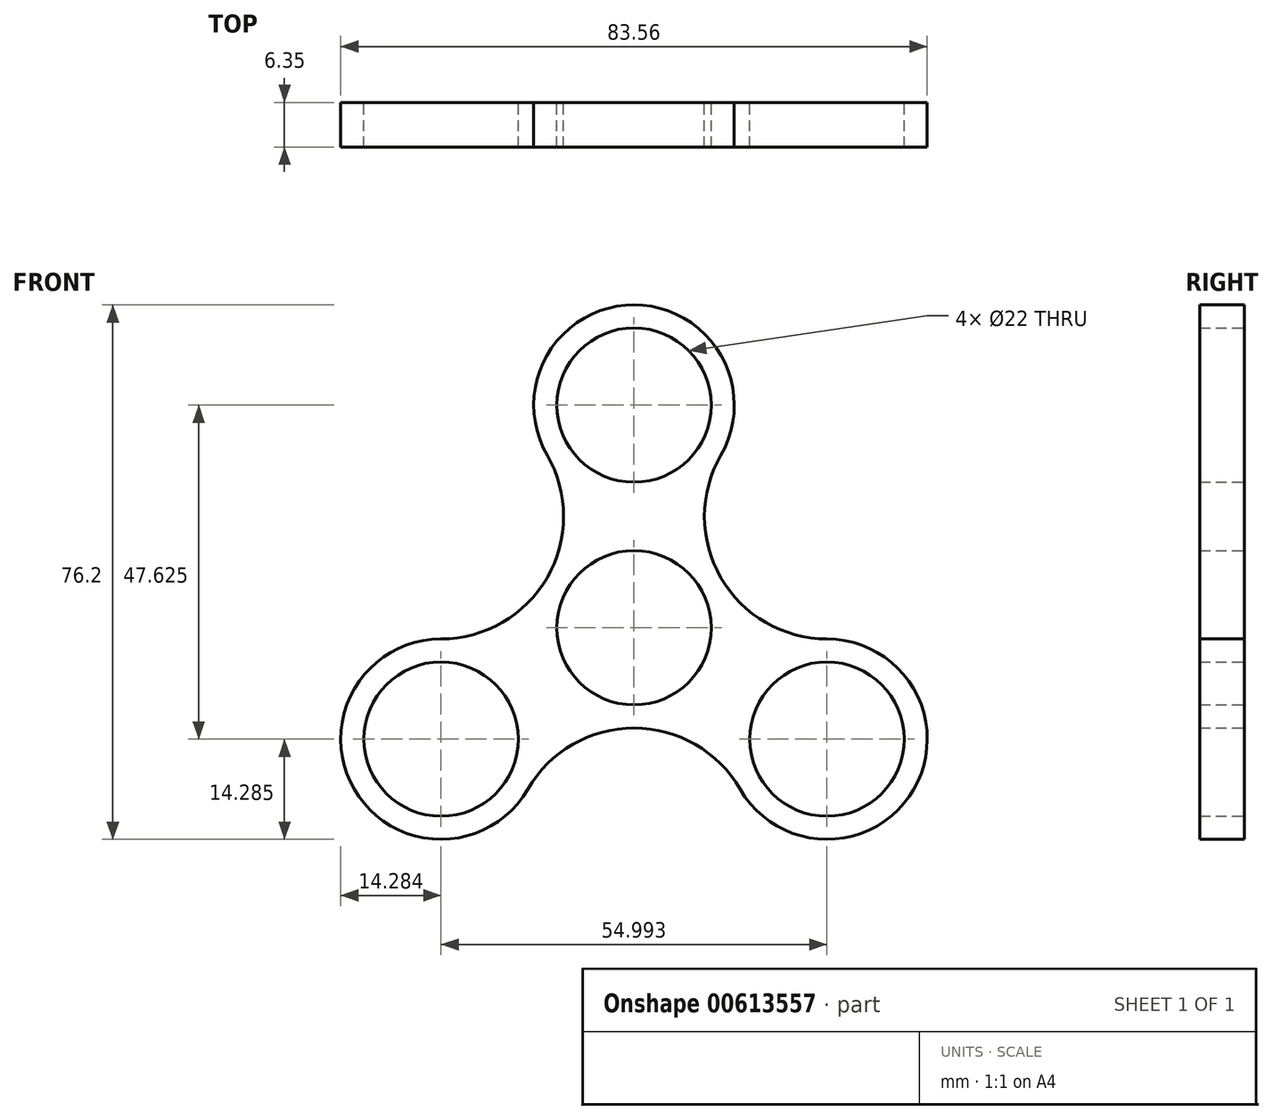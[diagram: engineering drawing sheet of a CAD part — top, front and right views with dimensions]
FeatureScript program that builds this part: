
annotation { "Feature Type Name" : "Feature", "Feature Type Description" : "" }
export const myFeature = defineFeature(function(context is Context, id is Id, definition is map)
    precondition{}
    {
        {
            var Q0;
            Q0=qCreatedBy(makeId("Front.planeOp"),FACE);
            var sketch = newSketch(context, id + "F0", { "sketchPlane" : qUnion([Q0])});
            skCircle(sketch, "E0", {"center": v(0, 0) * mm, "radius": 14.29 * mm});
            skCircle(sketch, "E1", {"center": v(0, 31.75) * mm, "radius": 14.29 * mm});
            skCircle(sketch, "E2", {"center": v(0, 31.75) * mm, "radius": 11 * mm});
            skCircle(sketch, "E3", {"center": v(0, 0) * mm, "radius": 11 * mm});
            skCircle(sketch, "E4.1.2", {"center": v(-27.5, -15.87) * mm, "radius": 14.29 * mm});
            skCircle(sketch, "E4.1.3", {"center": v(-27.5, -15.87) * mm, "radius": 11 * mm});
            skCircle(sketch, "E4.2.2", {"center": v(27.5, -15.88) * mm, "radius": 14.29 * mm});
            skCircle(sketch, "E4.2.3", {"center": v(27.5, -15.88) * mm, "radius": 11 * mm});
            skArc(sketch, "E5", {"start": v(-27.5, -1.59) * mm, "mid": v(-12.37, 7.14) * mm, "end": v(-12.37, 24.6) * mm});
            skArc(sketch, "E6", {"start": v(12.37, 24.6) * mm, "mid": v(12.37, 7.14) * mm, "end": v(27.5, -1.59) * mm});
            skArc(sketch, "E7", {"start": v(15.12, -23.02) * mm, "mid": v(0, -14.29) * mm, "end": v(-15.12, -23.02) * mm});
            skSolve(sketch);
        }
        {
            var Q0;
            {var subQ0=sQuery(id+"F0.wireOp",EDGE,"E5");var subQ1=sQuery(id+"F0.wireOp",EDGE,"E4.1.2");var subQ2=makeQuery(id+"F0.imprint","INTERSECT",VERTEX,{"derivedFrom":[subQ1,subQ0]});Q0=makeQuery(id+"F0.imprint","IMPRINT",FACE,{"disambiguationData":[TD([[makeQuery(id+"F0.imprint","IMPRINT",EDGE,{"disambiguationData":[TD([[subQ2,1.0]])],"derivedFrom":subQ1}),-1.0]])]});}
            var Q1;
            Q1=makeQuery(id+"F0.imprint","IMPRINT",FACE,{"disambiguationData":[TD([[makeQuery(id+"F0.imprint","IMPRINT",EDGE,{"derivedFrom":sQuery(id+"F0.wireOp",EDGE,"E4.1.3")}),-1.0]])]});
            var Q2;
            Q2=makeQuery(id+"F0.imprint","IMPRINT",FACE,{"disambiguationData":[TD([[makeQuery(id+"F0.imprint","IMPRINT",EDGE,{"derivedFrom":sQuery(id+"F0.wireOp",EDGE,"E3")}),-1.0]])]});
            var Q3;
            {var subQ0=sQuery(id+"F0.wireOp",EDGE,"E5");var subQ1=sQuery(id+"F0.wireOp",EDGE,"E1");var subQ2=makeQuery(id+"F0.imprint","INTERSECT",VERTEX,{"derivedFrom":[subQ1,subQ0]});Q3=makeQuery(id+"F0.imprint","IMPRINT",FACE,{"disambiguationData":[TD([[makeQuery(id+"F0.imprint","IMPRINT",EDGE,{"disambiguationData":[TD([[subQ2,-1.0]])],"derivedFrom":subQ1}),-1.0]])]});}
            var Q4;
            Q4=makeQuery(id+"F0.imprint","IMPRINT",FACE,{"disambiguationData":[TD([[makeQuery(id+"F0.imprint","IMPRINT",EDGE,{"derivedFrom":sQuery(id+"F0.wireOp",EDGE,"E2")}),-1.0]])]});
            var Q5;
            Q5=makeQuery(id+"F0.imprint","IMPRINT",FACE,{"disambiguationData":[TD([[makeQuery(id+"F0.imprint","IMPRINT",EDGE,{"derivedFrom":sQuery(id+"F0.wireOp",EDGE,"E4.2.3")}),-1.0]])]});
            var Q6;
            {var subQ0=sQuery(id+"F0.wireOp",EDGE,"E6");var subQ1=sQuery(id+"F0.wireOp",EDGE,"E0");var subQ2=makeQuery(id+"F0.imprint","INTERSECT",VERTEX,{"derivedFrom":[subQ1,subQ0]});Q6=makeQuery(id+"F0.imprint","IMPRINT",FACE,{"disambiguationData":[TD([[makeQuery(id+"F0.imprint","IMPRINT",EDGE,{"disambiguationData":[TD([[subQ2,1.0]])],"derivedFrom":subQ1}),-1.0]])]});}
            extrude(context, id + "F1", {"entities" : qUnion([Q0, Q1, Q2, Q3, Q4, Q5, Q6]), "depth" : 6.35 * mm, "offsetDistance" : 25.4 * mm});
        }
    });
